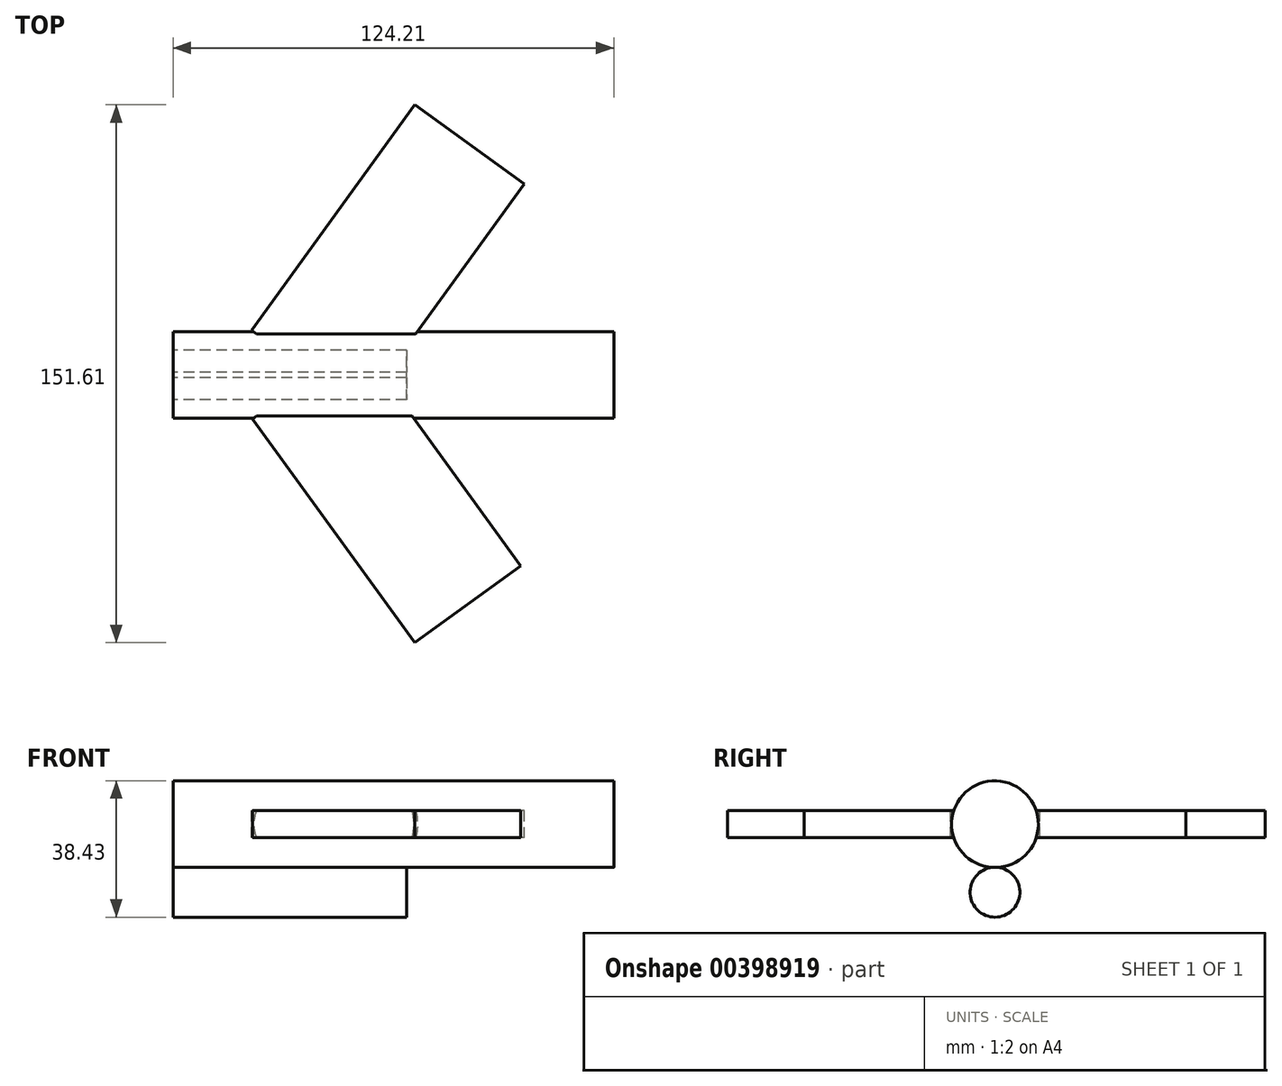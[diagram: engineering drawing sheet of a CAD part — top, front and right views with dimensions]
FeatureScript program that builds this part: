
annotation { "Feature Type Name" : "Feature", "Feature Type Description" : "" }
export const myFeature = defineFeature(function(context is Context, id is Id, definition is map)
    precondition{}
    {
        {
            var Q0;
            Q0=qCreatedBy(makeId("Right.planeOp"),FACE);
            var sketch = newSketch(context, id + "F0", { "sketchPlane" : qUnion([Q0])});
            skCircle(sketch, "E0", {"center": v(0, 0) * mm, "radius": 12.22 * mm});
            skSolve(sketch);
        }
        {
            var Q0;
            Q0=makeQuery(id+"F0.imprint","IMPRINT",FACE,{"disambiguationData":[TD([[makeQuery(id+"F0.imprint","IMPRINT",EDGE,{"derivedFrom":sQuery(id+"F0.wireOp",EDGE,"E0")}),1.0]])]});
            var Q1;
            Q1=sQuery(id+"F0.wireOp",EDGE,"E0");
            extrude(context, id + "F1", {"entities" : qUnion([Q0]), "surfaceEntities" : qUnion([Q1]), "depth" : 124.2 * mm});
        }
        {
            var Q0;
            Q0=qCreatedBy(makeId("Front.planeOp"),FACE);
            var sketch = newSketch(context, id + "F2", { "sketchPlane" : qUnion([Q0])});
            skLineSegment(sketch, "E1", {"start": v(96.63, 12.48) * mm, "end": v(123.61, 51.6) * mm});
            skLineSegment(sketch, "E2", {"start": v(123.61, 51.6) * mm, "end": v(123.61, 11.52) * mm});
            skSolve(sketch);
        }
        {
            var Q0;
            Q0=sQuery(id+"F2.wireOp",EDGE,"E1");
            var Q1;
            Q1=sQuery(id+"F2.wireOp",EDGE,"E2");
            extrude(context, id + "F3", {"bodyType" : ToolBodyType.SURFACE, "surfaceEntities" : qUnion([Q0, Q1]), "oppositeDirection" : true, "depth" : 3.05 * mm, "symmetric" : true});
        }
        {
            var Q0;
            Q0=qCreatedBy(makeId("Front.planeOp"),FACE);
            var sketch = newSketch(context, id + "F4", { "sketchPlane" : qUnion([Q0])});
            skFitSpline(sketch, "E3", {"points": [v(0, -11.59) * mm, v(-24.4, 0) * mm, v(0, 11.47) * mm, v(-9.1, 7.78) * mm], "startDerivative": vector(-106.66, 26.35) * mm, "endDerivative": vector(-66.71, -25.28) * mm});
            skSolve(sketch);
        }
        {
            var Q0;
            Q0=qCreatedBy(makeId("Top.planeOp"),FACE);
            var sketch = newSketch(context, id + "F5", { "sketchPlane" : qUnion([Q0])});
            skFitSpline(sketch, "E4", {"points": [v(0, 12.38) * mm, v(-24.5, 0) * mm, v(0, -12.23) * mm, v(0, -12.67) * mm], "startDerivative": vector(-87.86, -24.05) * mm, "endDerivative": vector(-4.92, -6.18) * mm});
            skSolve(sketch);
        }
        {
            var Q0;
            Q0=sQuery(id+"F5.wireOp",EDGE,"E4");
            extrude(context, id + "F6", {"bodyType" : ToolBodyType.SURFACE, "surfaceEntities" : qUnion([Q0]), "depth" : 7.62 * mm, "symmetric" : true});
        }
        {
            var Q0;
            Q0=sQuery(id+"F4.wireOp",EDGE,"E3");
            extrude(context, id + "F7", {"bodyType" : ToolBodyType.SURFACE, "surfaceEntities" : qUnion([Q0]), "depth" : 6.1 * mm, "symmetric" : true});
        }
        {
            var Q0;
            Q0=qCreatedBy(makeId("Top.planeOp"),FACE);
            var sketch = newSketch(context, id + "F8", { "sketchPlane" : qUnion([Q0])});
            skLineSegment(sketch, "E5", {"start": v(68.11, 12.09) * mm, "end": v(68.11, 76.19) * mm});
            skLineSegment(sketch, "E6", {"start": v(68.11, 76.19) * mm, "end": v(22.13, 12.65) * mm});
            skSolve(sketch);
        }
        {
            var Q0;
            Q0=qCreatedBy(makeId("Top.planeOp"),FACE);
            var sketch = newSketch(context, id + "F9", { "sketchPlane" : qUnion([Q0])});
            skLineSegment(sketch, "E7", {"start": v(68.11, -13) * mm, "end": v(68.11, -75.42) * mm});
            skLineSegment(sketch, "E8", {"start": v(68.11, -75.42) * mm, "end": v(22.4, -12.44) * mm});
            skSolve(sketch);
        }
        {
            var Q0;
            Q0=sQuery(id+"F9.wireOp",EDGE,"E8");
            var Q1;
            Q1=sQuery(id+"F9.wireOp",EDGE,"E7");
            extrude(context, id + "F10", {"bodyType" : ToolBodyType.SURFACE, "surfaceEntities" : qUnion([Q0, Q1]), "depth" : 7.62 * mm, "symmetric" : true});
        }
        {
            var Q0;
            Q0=sQuery(id+"F8.wireOp",EDGE,"E6");
            var Q1;
            Q1=sQuery(id+"F8.wireOp",EDGE,"E5");
            extrude(context, id + "F11", {"bodyType" : ToolBodyType.SURFACE, "surfaceEntities" : qUnion([Q0, Q1]), "depth" : 7.62 * mm, "symmetric" : true});
        }
        {
            var Q0;
            Q0=qCreatedBy(makeId("Front.planeOp"),FACE);
            var sketch = newSketch(context, id + "F12", { "sketchPlane" : qUnion([Q0])});
            skArc(sketch, "E9", {"start": v(46.53, 12.04) * mm, "mid": v(32.67, 25.79) * mm, "end": v(18.92, 11.93) * mm});
            skSolve(sketch);
        }
        {
            var Q0;
            Q0=sQuery(id+"F12.wireOp",EDGE,"E9");
            extrude(context, id + "F13", {"bodyType" : ToolBodyType.SURFACE, "surfaceEntities" : qUnion([Q0]), "oppositeDirection" : true, "depth" : 4.06 * mm, "symmetric" : true});
        }
        {
            var Q0;
            Q0=qCreatedBy(makeId("Right.planeOp"),FACE);
            var sketch = newSketch(context, id + "F14", { "sketchPlane" : qUnion([Q0])});
            skCircle(sketch, "E10", {"center": v(0, -19.18) * mm, "radius": 7.03 * mm});
            skSolve(sketch);
        }
        {
            var Q0;
            Q0 = qSketchRegion(id + "F14", true);
            extrude(context, id + "F15", {"entities" : qUnion([Q0]), "operationType" : NewBodyOperationType.ADD, "depth" : 65.8 * mm});
        }
        {
            var Q0;
            Q0=makeQuery(id+"F10.opExtrude","SWEPT_FACE",FACE,{"disambiguationData":[OSD([sQuery(id+"F9.wireOp",EDGE,"E8")])]});
            extrude(context, id + "F16", {"entities" : qUnion([Q0]), "operationType" : NewBodyOperationType.ADD, "depth" : 36.83 * mm});
        }
        {
            var Q0;
            Q0=makeQuery(id+"F11.opExtrude","SWEPT_FACE",FACE,{"disambiguationData":[OSD([sQuery(id+"F8.wireOp",EDGE,"E6")])]});
            extrude(context, id + "F17", {"entities" : qUnion([Q0]), "operationType" : NewBodyOperationType.ADD, "oppositeDirection" : true, "depth" : 38.1 * mm});
        }
    });
